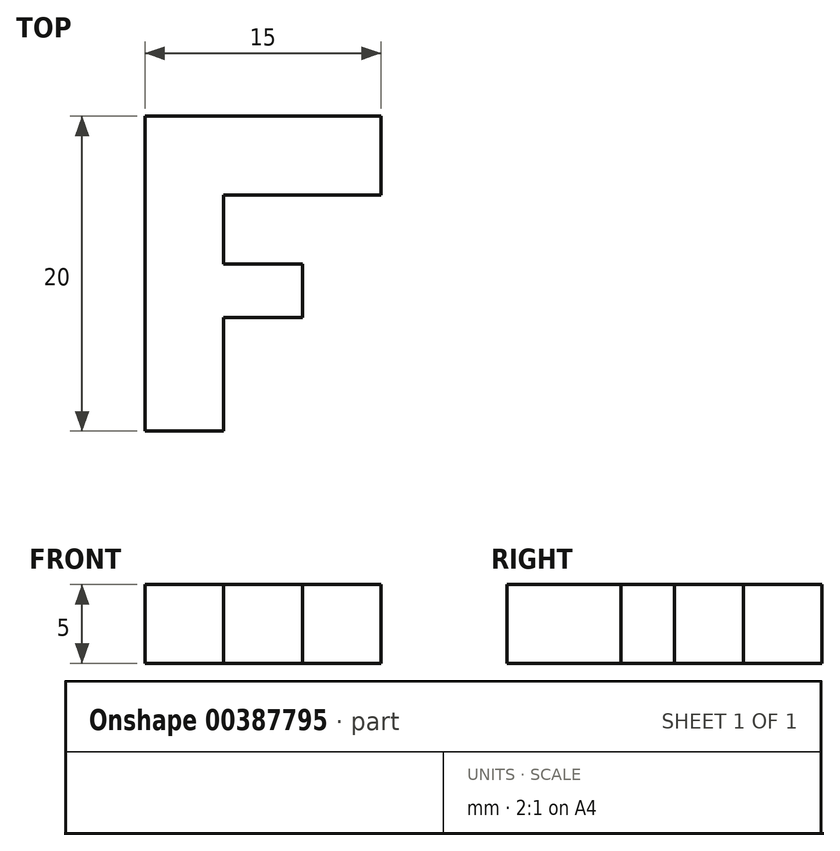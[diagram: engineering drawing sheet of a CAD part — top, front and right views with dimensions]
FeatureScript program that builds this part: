
annotation { "Feature Type Name" : "Feature", "Feature Type Description" : "" }
export const myFeature = defineFeature(function(context is Context, id is Id, definition is map)
    precondition{}
    {
        {
            var Q0;
            Q0=qCreatedBy(makeId("Top.planeOp"),FACE);
            var sketch = newSketch(context, id + "F0", { "sketchPlane" : qUnion([Q0])});
            skLineSegment(sketch, "E0", {"start": v(-6.33, 0.88) * mm, "end": v(-6.33, 20.88) * mm});
            skLineSegment(sketch, "E1", {"start": v(-6.33, 20.88) * mm, "end": v(8.67, 20.88) * mm});
            skLineSegment(sketch, "E2", {"start": v(8.67, 20.88) * mm, "end": v(8.67, 15.88) * mm});
            skLineSegment(sketch, "E3", {"start": v(8.67, 15.88) * mm, "end": v(-1.33, 15.88) * mm});
            skLineSegment(sketch, "E4", {"start": v(-1.33, 15.88) * mm, "end": v(-1.33, 11.5) * mm});
            skLineSegment(sketch, "E5", {"start": v(-1.33, 11.5) * mm, "end": v(3.67, 11.5) * mm});
            skLineSegment(sketch, "E6", {"start": v(3.67, 11.5) * mm, "end": v(3.67, 8.1) * mm});
            skLineSegment(sketch, "E7", {"start": v(3.67, 8.1) * mm, "end": v(-1.33, 8.1) * mm});
            skLineSegment(sketch, "E8", {"start": v(-1.33, 8.1) * mm, "end": v(-1.33, 0.88) * mm});
            skLineSegment(sketch, "E9", {"start": v(-1.33, 0.88) * mm, "end": v(-6.33, 0.88) * mm});
            skSolve(sketch);
        }
        {
            var Q0;
            Q0=makeQuery(id+"F0.imprint","IMPRINT",FACE,{"disambiguationData":[TD([[makeQuery(id+"F0.imprint","IMPRINT",EDGE,{"derivedFrom":sQuery(id+"F0.wireOp",EDGE,"E0")}),-1.0]])]});
            extrude(context, id + "F1", {"entities" : qUnion([Q0]), "depth" : 5 * mm});
        }
    });
